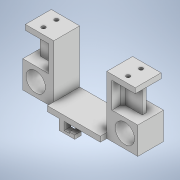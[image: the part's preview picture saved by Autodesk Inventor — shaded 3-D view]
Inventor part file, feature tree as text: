
AUTODESK INVENTOR PART (.ipt)
format: ipt  version: 2022 (Build 260153000, 153)  size: 208,896 bytes
history: native  units: mm
features: sketch x6, extrude x5, other x1, chamfer x1, hole x1
ambient origin geometry x8: Origin, YZ Plane, XZ Plane, XY Plane, X Axis, Y Axis, Z Axis, Center Point
bodies: Body1 (feature_tree), Body2 (feature_tree), Body3 (feature_tree)
feature tree (14):
  other  "Sólido1"
  extrude  "Extrusão1"  Depth=41.0mm
  extrude  "Extrusão2"  Depth=8.0mm
  extrude  "Extrusão3"  Depth=2.0mm
  extrude  "Extrusão4"  Depth=4.0mm
  chamfer  "Chanfro1"  Distance=15.0mm
  hole  "Furo1"  [1 undecoded]
  extrude  "Extrusão6"  Depth=2.0mm TaperAngle=45.0deg
  sketch  "Esboço1"  dims[d7=20.0mm d8=0.0mm d9=41.0mm]
  sketch  "Esboço2"  dims[d10=5.0mm d11=0.0mm d12=8.0mm]
  sketch  "Esboço3"  dims[d13=10.0mm d14=2.0mm]
  sketch  "Esboço5"  dims[d15=3.0mm d16=4.0mm]
  sketch  "Esboço7"  dims[d17=1.0mm]
  sketch  "Esboço8"  dims[d18=4.0mm d22=15.0mm d23=0.0mm d24=15.0mm d25=0.0mm d28=2.0mm d29=2.0mm d30=45.0deg d31=3.0mm d32=6.0mm d33=4.0mm d34=2.0mm d35=90.0deg d36=8.0mm d37=20.594885mm d38=20.0mm d39=20.0mm d40=15.0mm d41=15.0mm d42=10.0mm d43=0.0mm d44=5.0mm d45=5.0mm d46=5.0mm d47=5.0mm]
note: 1 required parameter value undecoded (feature->parameter linkage not recoverable at this tier; creation-order binding heuristic only, values carry confidence <= 0.55)
